# Revit family: Pendant PLED10
name_source: partatom
category: Lighting Fixtures
revit_build: Autodesk Revit 2014 (Build: 20130709_2115(x64)
units: mm (PartAtom-declared; Revit-internal decimal feet)

## types (1)
- Base Type
    ANSI Lamp Spec = Default - Load Type Catalog
    Absolute Color Temperature = 0 K
    Anchor Bolts = Default - Load Type Catalog
    Apparent Load = 0 VA
    Assembly Code = D5020200
    Avg Rated Life - TM21 Life Expectancy = Default - Load Type Catalog
    BUG Rating = Default - Load Type Catalog
    Ballast / Driver Circuit = Default - Load Type Catalog
    Ballast Factor = 0
    Ballast ID / ANSI Spec = Default - Load Type Catalog
    Base Configuration = Default - Load Type Catalog
    Beam Efficiency % = Default - Load Type Catalog
    Bolt Circle = Default - Load Type Catalog
    CIE Type = Default - Load Type Catalog
    CRI 9 = Default - Load Type Catalog
    CRI a = Default - Load Type Catalog
    Connector Description = Default - Load Type Catalog
    Cost = 0 $
    Cutoff Classification = Default - Load Type Catalog
    Data Datecode = Date Revit Family Type was Created
    Default Elevation = 4' - 0"
    Description = Default - Load Type Catalog
    Field Efficiency = Default - Load Type Catalog
    Fixture EPA Rating = Default - Load Type Catalog
    Fixture Finish = <By Category>
    Fixture Weight lbs. = Default - Load Type Catalog
    Glass = <By Category>
    Horizontal Beam Angle Degrees = 0
    Horizontial Field Angle Degrees = 0
    IES Classification = Default - Load Type Catalog
    IP Rating = Default - Load Type Catalog
    Initial Source Lumens = 0 lm
    Input Wattage = 0 W
    Keynote = Division 26
    Lamp = Default - Load Type Catalog
    Lamp Base = Default - Load Type Catalog
    Lamp Envelop = Default - Load Type Catalog
    Lensing / Control Media = Default - Load Type Catalog
    Longitudinal Classification = Default - Load Type Catalog
    Lumens per Watt = 0 lm/W
    Luminiare Efficacy Rating LER = 0 lm/W
    Luminious Aperture Appearance = <By Category>
    Manufacturer = RAB Lighting, Inc.
    Master Foramt 2004 (Keynote) = Default - Load Type Catalog
    Masterformat 2004 Divison of Work = Default - Load Type Catalog
    Max Ambient Temp = 104 °F
    Max Pole EPA Rating = Default - Load Type Catalog
    Mean Source Lumens or L70 Point = 0 lm
    Min Starting Temp = -40 °F
    Model = Default - Load Type Catalog
    Mounting Configuration = Default - Load Type Catalog
    NEMA Type = Default - Load Type Catalog
    Nominal Color Temperature = 0 K
    Nominal Wattage = 0 W
    Number of Drivers = Default - Load Type Catalog
    Operating Amps = 0 A
    Photometric File Name = Default - Load Type Catalog
    Pole Finish = <By Category>
    Pole Wall Thickness ga. = Default - Load Type Catalog
    Product Description = Default - Load Type Catalog
    Product Line = Default - Load Type Catalog
    Product Model Number = Default - Load Type Catalog
    RAB Ballast / Driver ID = Default - Load Type Catalog
    Source = Default - Load Type Catalog
    Spacing Criteria 0-180 = 0
    Spacing Criteria 90-270 = 0
    Spacing Criteria Diagonal = 0
    Starting Amps = 0 A
    Surge Protection kV = 0 V
    THD = Default - Load Type Catalog
    Total Lumnaire Efficiency = Default - Load Type Catalog
    Type Comments = Default - Load Type Catalog
    UL / ULC Listing = Default - Load Type Catalog
    URL = www.rabled.com
    URL Alternate 1 = www.rabweb.com
    URL Alternate 2 = www.rabweb.com
    Uniformat II (Assembly Code) = Default - Load Type Catalog
    Uniformat II Description = Default - Load Type Catalog
    Vertical Beam Angle Degrees = 0
    Vertical Field Angle Degrees = 0
    Voltage = 0 V
    Wattage Comments = 0

## geometry (parser evidence)
native form markers: Sweep x20
no freeform markers — native parametric forms only
